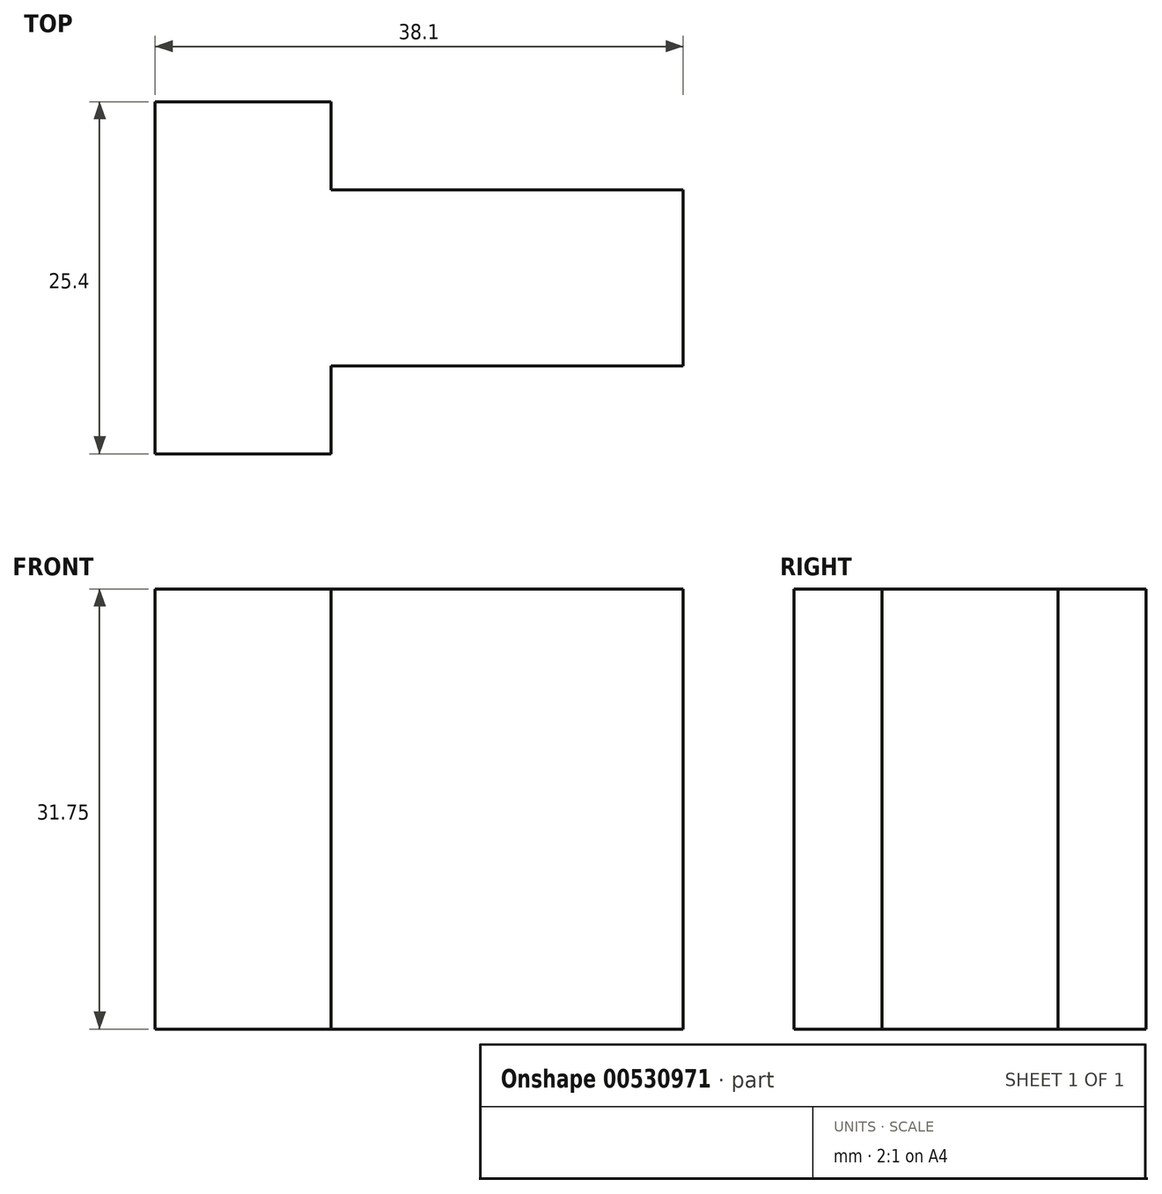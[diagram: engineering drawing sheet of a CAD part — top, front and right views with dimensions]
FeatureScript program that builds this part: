
annotation { "Feature Type Name" : "Feature", "Feature Type Description" : "" }
export const myFeature = defineFeature(function(context is Context, id is Id, definition is map)
    precondition{}
    {
        {
            var Q0;
            Q0=qCreatedBy(makeId("Top.planeOp"),FACE);
            var sketch = newSketch(context, id + "F0", { "sketchPlane" : qUnion([Q0])});
            skLineSegment(sketch, "E0", {"start": v(0, 0) * mm, "end": v(0, 25.4) * mm});
            skLineSegment(sketch, "E1", {"start": v(0, 25.4) * mm, "end": v(12.7, 25.4) * mm});
            skLineSegment(sketch, "E2", {"start": v(12.7, 25.4) * mm, "end": v(12.7, 19.05) * mm});
            skLineSegment(sketch, "E3", {"start": v(12.7, 19.05) * mm, "end": v(38.1, 19.05) * mm});
            skLineSegment(sketch, "E4", {"start": v(38.1, 19.05) * mm, "end": v(38.1, 6.35) * mm});
            skLineSegment(sketch, "E5", {"start": v(38.1, 6.35) * mm, "end": v(12.7, 6.35) * mm});
            skLineSegment(sketch, "E6", {"start": v(12.7, 6.35) * mm, "end": v(12.7, 0) * mm});
            skLineSegment(sketch, "E7", {"start": v(12.7, 0) * mm, "end": v(0, 0) * mm});
            skSolve(sketch);
        }
        {
            var Q0;
            Q0=makeQuery(id+"F0.imprint","IMPRINT",FACE,{"disambiguationData":[TD([[makeQuery(id+"F0.imprint","IMPRINT",EDGE,{"derivedFrom":sQuery(id+"F0.wireOp",EDGE,"E0")}),-1.0]])]});
            extrude(context, id + "F1", {"entities" : qUnion([Q0]), "depth" : 31.75 * mm, "offsetDistance" : 25.4 * mm});
        }
    });
